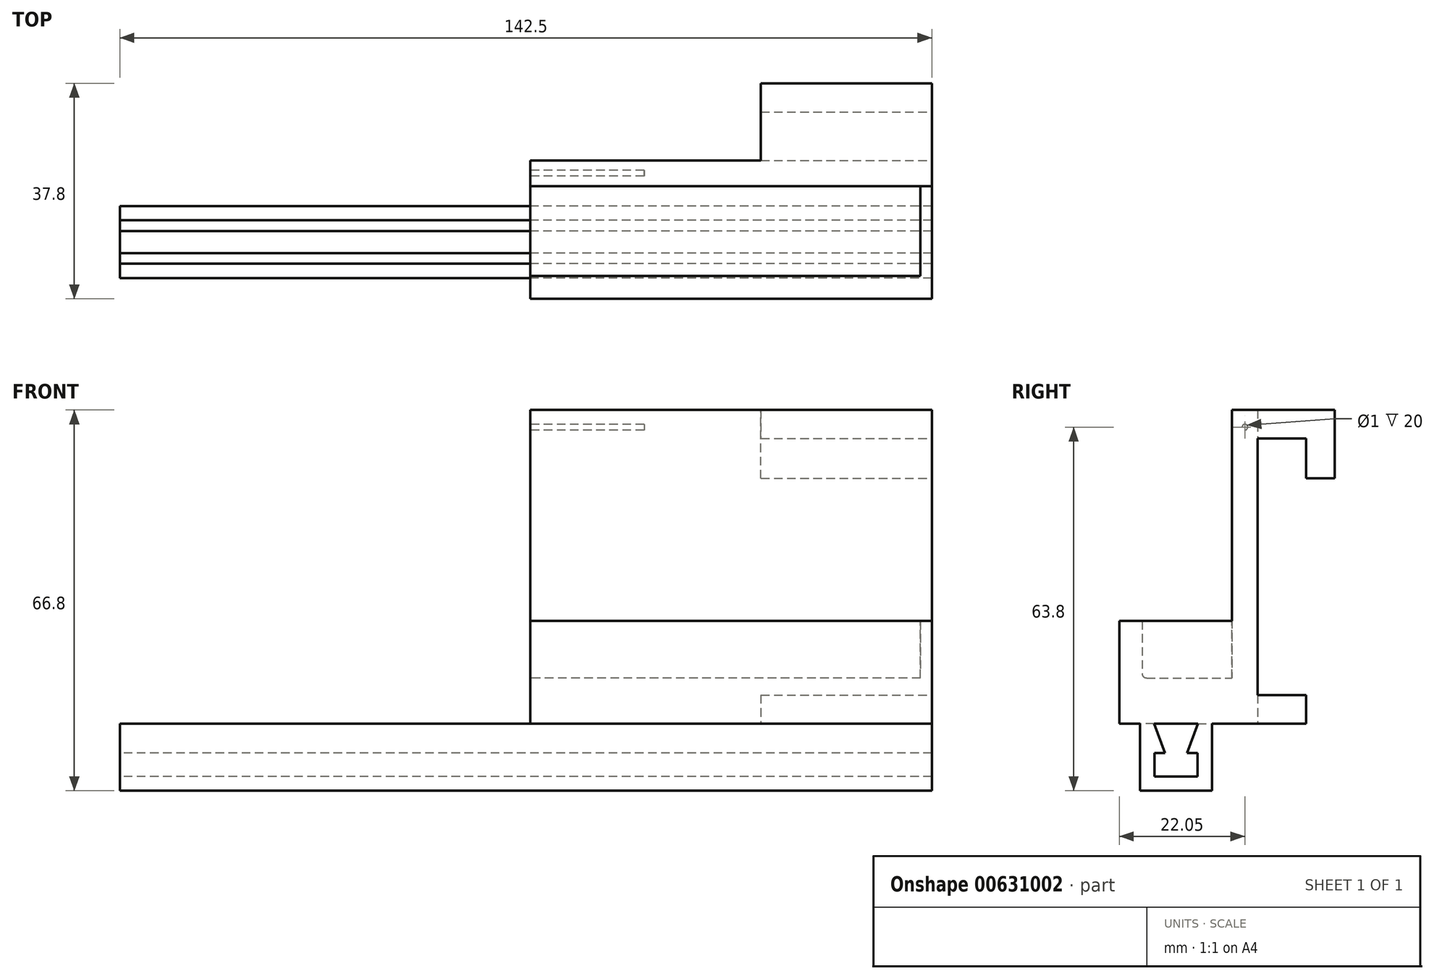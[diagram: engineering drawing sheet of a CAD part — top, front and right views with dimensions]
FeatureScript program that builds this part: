
annotation { "Feature Type Name" : "Feature", "Feature Type Description" : "" }
export const myFeature = defineFeature(function(context is Context, id is Id, definition is map)
    precondition{}
    {
        {
            var Q0;
            Q0=qCreatedBy(makeId("Front.planeOp"),FACE);
            var sketch = newSketch(context, id + "F0", { "sketchPlane" : qUnion([Q0])});
            skLineSegment(sketch, "E0.bottom", {"start": v(-77.5, -27.5) * mm, "end": v(77.5, -27.5) * mm});
            skLineSegment(sketch, "E0.top", {"start": v(-77.5, 27.5) * mm, "end": v(77.5, 27.5) * mm});
            skLineSegment(sketch, "E0.left", {"start": v(-77.5, -27.5) * mm, "end": v(-77.5, 27.5) * mm});
            skLineSegment(sketch, "E0.right", {"start": v(77.5, -27.5) * mm, "end": v(77.5, 27.5) * mm});
            skSolve(sketch);
        }
        {
            var Q0;
            Q0=makeQuery(id+"F0.imprint","IMPRINT",FACE,{"disambiguationData":[TD([[makeQuery(id+"F0.imprint","IMPRINT",EDGE,{"derivedFrom":sQuery(id+"F0.wireOp",EDGE,"E0.bottom")}),1.0]])]});
            extrude(context, id + "F1", {"entities" : qUnion([Q0]), "depth" : 13 * mm, "offsetDistance" : 25 * mm});
        }
        {
            var Q0;
            Q0=makeQuery(id+"F1.opExtrude","CAP_FACE",FACE,{"disambiguationData":[OSD([sQuery(id+"F0.wireOp",EDGE,"E0.bottom"),sQuery(id+"F0.wireOp",EDGE,"E0.top"),sQuery(id+"F0.wireOp",EDGE,"E0.left"),sQuery(id+"F0.wireOp",EDGE,"E0.right")])],"isStart":true});
            var sketch = newSketch(context, id + "F2", { "sketchPlane" : qUnion([Q0])});
            skLineSegment(sketch, "E1.bottom", {"start": v(77.5, -22.5) * mm, "end": v(47.5, -22.5) * mm});
            skLineSegment(sketch, "E1.top", {"start": v(77.5, 22.5) * mm, "end": v(47.5, 22.5) * mm});
            skLineSegment(sketch, "E1.left", {"start": v(77.5, -22.5) * mm, "end": v(77.5, 22.5) * mm});
            skLineSegment(sketch, "E1.right", {"start": v(-77.5, -22.5) * mm, "end": v(-77.5, 22.5) * mm});
            skPoint(sketch, "E1.middle", {"position": v(0, 0) * mm});
            skLineSegment(sketch, "E2.trimOffspring", {"start": v(-47.5, 22.5) * mm, "end": v(-77.5, 22.5) * mm});
            skLineSegment(sketch, "E3.trimOffspring", {"start": v(-47.5, -22.5) * mm, "end": v(-77.5, -22.5) * mm});
            skLineSegment(sketch, "E4", {"start": v(-47.5, 22.5) * mm, "end": v(47.5, 22.5) * mm});
            skLineSegment(sketch, "E5", {"start": v(-47.5, -22.5) * mm, "end": v(47.5, -22.5) * mm});
            skSolve(sketch);
        }
        {
            var Q0;
            Q0=makeQuery(id+"F2.imprint","IMPRINT",FACE,{"disambiguationData":[TD([[makeQuery(id+"F2.imprint","IMPRINT",EDGE,{"derivedFrom":sQuery(id+"F2.wireOp",EDGE,"E1.bottom")}),-1.0]])]});
            extrude(context, id + "F3", {"entities" : qUnion([Q0]), "operationType" : NewBodyOperationType.REMOVE, "oppositeDirection" : true, "depth" : 8.5 * mm, "offsetDistance" : 25 * mm});
        }
        {
            var Q0;
            Q0=makeQuery(id+"F3.boolean.opBoolean","COPY",FACE,{"derivedFrom":makeQuery(id+"F3.opExtrude","CAP_FACE",FACE,{"disambiguationData":[OSD([sQuery(id+"F2.wireOp",EDGE,"E1.bottom"),sQuery(id+"F2.wireOp",EDGE,"E1.top"),sQuery(id+"F2.wireOp",EDGE,"E1.left"),sQuery(id+"F2.wireOp",EDGE,"E1.right"),sQuery(id+"F2.wireOp",EDGE,"E2.trimOffspring"),sQuery(id+"F2.wireOp",EDGE,"E3.trimOffspring"),sQuery(id+"F2.wireOp",EDGE,"E4"),sQuery(id+"F2.wireOp",EDGE,"E5")])],"isStart":false})});
            var sketch = newSketch(context, id + "F4", { "sketchPlane" : qUnion([Q0])});
            skLineSegment(sketch, "E6", {"start": v(-47.5, 27.5) * mm, "end": v(-47.5, -27.5) * mm});
            skLineSegment(sketch, "E7", {"start": v(47.5, 27.5) * mm, "end": v(47.5, -27.5) * mm});
            skLineSegment(sketch, "E8", {"start": v(-47.5, 27.5) * mm, "end": v(47.5, 27.5) * mm});
            skLineSegment(sketch, "E9", {"start": v(-47.5, -27.5) * mm, "end": v(47.5, -27.5) * mm});
            skSolve(sketch);
        }
        {
            var Q0;
            Q0=qSketchRegion(id+"F4",true);
            extrude(context, id + "F5", {"entities" : qUnion([Q0]), "operationType" : NewBodyOperationType.REMOVE, "depth" : 8.5 * mm, "offsetDistance" : 25 * mm});
        }
        {
            var Q0;
            Q0=makeQuery(id+"F1.opExtrude","SWEPT_FACE",FACE,{"disambiguationData":[OSD([sQuery(id+"F0.wireOp",EDGE,"E0.top")])]});
            var sketch = newSketch(context, id + "F6", { "sketchPlane" : qUnion([Q0])});
            skLineSegment(sketch, "E10.bottom", {"start": v(-77.5, 0) * mm, "end": v(-47.5, 0) * mm});
            skLineSegment(sketch, "E10.top", {"start": v(-77.5, 5) * mm, "end": v(-47.5, 5) * mm});
            skLineSegment(sketch, "E10.left", {"start": v(-77.5, 0) * mm, "end": v(-77.5, 5) * mm});
            skLineSegment(sketch, "E10.right", {"start": v(-47.5, 0) * mm, "end": v(-47.5, 5) * mm});
            skLineSegment(sketch, "E11.bottom", {"start": v(47.5, 0) * mm, "end": v(77.5, 0) * mm});
            skLineSegment(sketch, "E11.top", {"start": v(47.5, 5) * mm, "end": v(77.5, 5) * mm});
            skLineSegment(sketch, "E11.left", {"start": v(47.5, 0) * mm, "end": v(47.5, 5) * mm});
            skLineSegment(sketch, "E11.right", {"start": v(77.5, 0) * mm, "end": v(77.5, 5) * mm});
            skSolve(sketch);
        }
        {
            var Q0;
            Q0=qSketchRegion(id+"F6",true);
            extrude(context, id + "F7", {"entities" : qUnion([Q0]), "operationType" : NewBodyOperationType.ADD, "oppositeDirection" : true, "depth" : (8 + 4) * mm, "offsetDistance" : 25 * mm});
        }
        {
            var Q0;
            {var subQ0=sQuery(id+"F6.wireOp",EDGE,"E10.left");Q0=makeQuery(id+"FyL1myXJDopJi9Z_1.1.F7.boolean.opBoolean","MERGE",FACE,{"derivedFrom":[makeQuery(id+"F7.boolean.opBoolean","MERGE",FACE,{"derivedFrom":[makeQuery(id+"F1.opExtrude","SWEPT_FACE",FACE,{"disambiguationData":[OSD([sQuery(id+"F0.wireOp",EDGE,"E0.left")])]}),makeQuery(id+"F7.opExtrude","SWEPT_FACE",FACE,{"disambiguationData":[OSD([subQ0])]})]}),makeQuery(id+"FyL1myXJDopJi9Z_1.1.F7.opExtrude","SWEPT_FACE",FACE,{"disambiguationData":[OSD([subQ0])]})]});}
            var sketch = newSketch(context, id + "F8", { "sketchPlane" : qUnion([Q0])});
            skLineSegment(sketch, "E12", {"start": v(13, -27.5) * mm, "end": v(28.8, -27.5) * mm});
            skLineSegment(sketch, "E13", {"start": v(28.8, -18.7) * mm, "end": v(28.8, -9.5) * mm});
            skLineSegment(sketch, "E14", {"start": v(28.8, -9.5) * mm, "end": v(32.8, -9.5) * mm});
            skLineSegment(sketch, "E15", {"start": v(32.8, -9.5) * mm, "end": v(32.8, -27.5) * mm});
            skLineSegment(sketch, "E16", {"start": v(32.8, -27.5) * mm, "end": v(28.8, -27.5) * mm});
            skLineSegment(sketch, "E17", {"start": v(13, -19.5) * mm, "end": v(28, -19.5) * mm});
            skLineSegment(sketch, "E18", {"start": v(13, -19.5) * mm, "end": v(13, -27.5) * mm});
            skPoint(sketch, "E19.visualSharp", {"position": v(28.8, -19.5) * mm});
            skArc(sketch, "E19.filletArc", {"start": v(28, -19.5) * mm, "mid": v(28.57, -19.27) * mm, "end": v(28.8, -18.7) * mm});
            skSolve(sketch);
        }
        {
            var Q0;
            Q0=makeQuery(id+"F8.imprint","IMPRINT",FACE,{"disambiguationData":[TD([[makeQuery(id+"F8.imprint","IMPRINT",EDGE,{"derivedFrom":sQuery(id+"F8.wireOp",EDGE,"E12")}),1.0]])]});
            var Q1;
            {var subQ0=sQuery(id+"F6.wireOp",EDGE,"E11.right");Q1=makeQuery(id+"FyL1myXJDopJi9Z_1.1.F7.boolean.opBoolean","MERGE",FACE,{"derivedFrom":[makeQuery(id+"F7.boolean.opBoolean","MERGE",FACE,{"derivedFrom":[makeQuery(id+"F1.opExtrude","SWEPT_FACE",FACE,{"disambiguationData":[OSD([sQuery(id+"F0.wireOp",EDGE,"E0.right")])]}),makeQuery(id+"F7.opExtrude","SWEPT_FACE",FACE,{"disambiguationData":[OSD([subQ0])]})]}),makeQuery(id+"FyL1myXJDopJi9Z_1.1.F7.opExtrude","SWEPT_FACE",FACE,{"disambiguationData":[OSD([subQ0])]})]});}
            extrude(context, id + "F9", {"entities" : qUnion([Q0]), "operationType" : NewBodyOperationType.ADD, "endBound" : BoundingType.UP_TO_SURFACE, "oppositeDirection" : true, "depth" : 25 * mm, "endBoundEntityFace" : qUnion([Q1]), "offsetDistance" : 25 * mm});
        }
        {
            var Q0;
            {var subQ0=sQuery(id+"F6.wireOp",EDGE,"E10.left");Q0=makeQuery(id+"F9.boolean.opBoolean","MERGE",FACE,{"derivedFrom":[makeQuery(id+"FyL1myXJDopJi9Z_1.1.F7.boolean.opBoolean","MERGE",FACE,{"derivedFrom":[makeQuery(id+"F7.boolean.opBoolean","MERGE",FACE,{"derivedFrom":[makeQuery(id+"F1.opExtrude","SWEPT_FACE",FACE,{"disambiguationData":[OSD([sQuery(id+"F0.wireOp",EDGE,"E0.left")])]}),makeQuery(id+"F7.opExtrude","SWEPT_FACE",FACE,{"disambiguationData":[OSD([subQ0])]})]}),makeQuery(id+"FyL1myXJDopJi9Z_1.1.F7.opExtrude","SWEPT_FACE",FACE,{"disambiguationData":[OSD([subQ0])]})]}),makeQuery(id+"F9.opExtrude","CAP_FACE",FACE,{"disambiguationData":[OSD([sQuery(id+"F8.wireOp",EDGE,"E12"),sQuery(id+"F8.wireOp",EDGE,"E13"),sQuery(id+"F8.wireOp",EDGE,"E14"),sQuery(id+"F8.wireOp",EDGE,"E15"),sQuery(id+"F8.wireOp",EDGE,"E16"),sQuery(id+"F8.wireOp",EDGE,"E17"),sQuery(id+"F8.wireOp",EDGE,"E18"),sQuery(id+"F8.wireOp",EDGE,"E19.filletArc")])],"isStart":true})]});}
            var sketch = newSketch(context, id + "F10", { "sketchPlane" : qUnion([Q0])});
            skLineSegment(sketch, "E20", {"start": v(19.33, -33) * mm, "end": v(19.33, -36.5) * mm});
            skLineSegment(sketch, "E21", {"start": v(19.33, -36.5) * mm, "end": v(26.33, -36.5) * mm});
            skLineSegment(sketch, "E22", {"start": v(26.33, -36.5) * mm, "end": v(26.33, -33) * mm});
            skLineSegment(sketch, "E23", {"start": v(26.33, -27.5) * mm, "end": v(19.33, -27.5) * mm});
            skLineSegment(sketch, "E24", {"start": v(19.33, -33) * mm, "end": v(21.33, -33) * mm});
            skLineSegment(sketch, "E25", {"start": v(21.33, -33) * mm, "end": v(19.33, -27.5) * mm});
            skLineSegment(sketch, "E26", {"start": v(22.83, -36.5) * mm, "end": v(22.83, -27.5) * mm, "construction": true});
            skLineSegment(sketch, "E27.MirrorCS", {"start": v(24.33, -33) * mm, "end": v(26.33, -27.5) * mm});
            skLineSegment(sketch, "E28.MirrorCS", {"start": v(26.33, -33) * mm, "end": v(24.33, -33) * mm});
            skLineSegment(sketch, "E29.MirrorCS", {"start": v(26.33, -33) * mm, "end": v(26.33, -36.5) * mm});
            skLineSegment(sketch, "E30", {"start": v(19.33, -33) * mm, "end": v(19.33, -36.5) * mm, "construction": true});
            skPoint(sketch, "E31.orphan", {"position": v(26.33, -27.5) * mm});
            skSolve(sketch);
        }
        {
            var Q0;
            Q0=qCreatedBy(makeId("Right.planeOp"),FACE);
            cPlane(context, id + "F11", {"entities" : qUnion([Q0]), "cplaneType" : CPlaneType.OFFSET, "offset" : 30 * mm, "oppositeDirection" : true, "width" : 150 * mm, "height" : 150 * mm});
        }
        {
            var Q0;
            Q0=qCreatedBy(id+"F11.planeOp",FACE);
            var sketch = newSketch(context, id + "F12", { "sketchPlane" : qUnion([Q0])});
            skLineSegment(sketch, "E32.0", {"start": v(-19.33, -36.5) * mm, "end": v(-26.33, -36.5) * mm, "construction": true});
            skLineSegment(sketch, "E33.0", {"start": v(-19.33, -33) * mm, "end": v(-19.33, -36.5) * mm, "construction": true});
            skLineSegment(sketch, "E34.0", {"start": v(-19.33, -33) * mm, "end": v(-21.33, -33) * mm, "construction": true});
            skLineSegment(sketch, "E35.0", {"start": v(-21.33, -33) * mm, "end": v(-19.33, -27.5) * mm, "construction": true});
            skLineSegment(sketch, "E36.0", {"start": v(-24.33, -33) * mm, "end": v(-26.33, -27.5) * mm, "construction": true});
            skLineSegment(sketch, "E37.0", {"start": v(-26.33, -33) * mm, "end": v(-24.33, -33) * mm, "construction": true});
            skLineSegment(sketch, "E38.0", {"start": v(-26.33, -33) * mm, "end": v(-26.33, -36.5) * mm, "construction": true});
            skLineSegment(sketch, "E39", {"start": v(-19.01, -27.5) * mm, "end": v(-19.33, -27.5) * mm});
            skLineSegment(sketch, "E40.0", {"start": v(-20.9, -32.7) * mm, "end": v(-19.01, -27.5) * mm});
            skLineSegment(sketch, "E41.0", {"start": v(-19.03, -32.7) * mm, "end": v(-19.03, -36.8) * mm});
            skLineSegment(sketch, "E42.0", {"start": v(-26.63, -32.7) * mm, "end": v(-26.63, -36.8) * mm});
            skLineSegment(sketch, "E43.0", {"start": v(-26.63, -32.7) * mm, "end": v(-24.76, -32.7) * mm});
            skLineSegment(sketch, "E44.0", {"start": v(-19.03, -32.7) * mm, "end": v(-20.9, -32.7) * mm});
            skLineSegment(sketch, "E45.0", {"start": v(-19.03, -36.8) * mm, "end": v(-26.63, -36.8) * mm});
            skLineSegment(sketch, "E46.trimOffspring", {"start": v(-24.76, -32.7) * mm, "end": v(-26.65, -27.5) * mm});
            skLineSegment(sketch, "E47", {"start": v(-19.01, -27.5) * mm, "end": v(-16.51, -27.5) * mm});
            skLineSegment(sketch, "E48", {"start": v(-16.51, -27.5) * mm, "end": v(-16.51, -39.3) * mm});
            skLineSegment(sketch, "E49", {"start": v(-16.51, -39.3) * mm, "end": v(-29.15, -39.3) * mm});
            skLineSegment(sketch, "E50", {"start": v(-29.15, -39.3) * mm, "end": v(-29.15, -27.5) * mm});
            skLineSegment(sketch, "E51", {"start": v(-16.51, -27.5) * mm, "end": v(-19.01, -27.5) * mm});
            skLineSegment(sketch, "E52", {"start": v(-26.65, -27.5) * mm, "end": v(-29.15, -27.5) * mm});
            skLineSegment(sketch, "E53.trimOffspring", {"start": v(-26.33, -27.5) * mm, "end": v(-26.65, -27.5) * mm});
            skSolve(sketch);
        }
        {
            var Q0;
            Q0=qSketchRegion(id+"F12",true);
            var Q1;
            {var subQ0=sQuery(id+"F6.wireOp",EDGE,"E11.right");var subQ1=sQuery(id+"F0.wireOp",EDGE,"E0.right");Q1=makeQuery(id+"F9.boolean.opBoolean","MERGE",FACE,{"derivedFrom":[makeQuery(id+"FyL1myXJDopJi9Z_1.1.F7.boolean.opBoolean","MERGE",FACE,{"derivedFrom":[makeQuery(id+"F7.boolean.opBoolean","MERGE",FACE,{"derivedFrom":[makeQuery(id+"F1.opExtrude","SWEPT_FACE",FACE,{"disambiguationData":[OSD([subQ1])]}),makeQuery(id+"F7.opExtrude","SWEPT_FACE",FACE,{"disambiguationData":[OSD([subQ0])]})]}),makeQuery(id+"FyL1myXJDopJi9Z_1.1.F7.opExtrude","SWEPT_FACE",FACE,{"disambiguationData":[OSD([subQ0])]})]}),makeQuery(id+"F9.opExtrude","CAP_FACE",FACE,{"disambiguationData":[OSD([subQ1,subQ0])],"isStart":false})]});}
            extrude(context, id + "F13", {"entities" : qUnion([Q0]), "operationType" : NewBodyOperationType.ADD, "endBound" : BoundingType.UP_TO_SURFACE, "depth" : 86.6 * mm, "endBoundEntityFace" : qUnion([Q1]), "offsetDistance" : 25 * mm});
        }
        {
            var Q0;
            Q0=makeQuery(id+"F9.opExtrude","SWEPT_FACE",FACE,{"disambiguationData":[OSD([sQuery(id+"F8.wireOp",EDGE,"E15")])]});
            var sketch = newSketch(context, id + "F14", { "sketchPlane" : qUnion([Q0])});
            skLineSegment(sketch, "E54.bottom", {"start": v(33.5, 67.48) * mm, "end": v(115.57, 67.48) * mm});
            skLineSegment(sketch, "E54.top", {"start": v(33.5, -48.03) * mm, "end": v(115.57, -48.03) * mm});
            skLineSegment(sketch, "E54.left", {"start": v(33.5, 67.48) * mm, "end": v(33.5, -48.03) * mm});
            skLineSegment(sketch, "E54.right", {"start": v(115.57, 67.48) * mm, "end": v(115.57, -48.03) * mm});
            skSolve(sketch);
        }
        {
            var Q0;
            {var subQ1=sQuery(id+"F8.wireOp",EDGE,"E15");var subQ6=makeQuery(id+"F9.opExtrude","CAP_EDGE",EDGE,{"disambiguationData":[OSD([subQ1])],"isStart":true});Q0=makeQuery(id+"F14.imprint","IMPRINT",FACE,{"disambiguationData":[TD([[makeQuery(id+"F14.imprint","IMPRINT",EDGE,{"derivedFrom":subQ6}),1.0]])]});}
            var sketch = newSketch(context, id + "F15", { "sketchPlane" : qUnion([Q0])});
            skLineSegment(sketch, "E55.bottom", {"start": v(-107.56, 91.1) * mm, "end": v(7, 91.1) * mm});
            skLineSegment(sketch, "E55.top", {"start": v(-107.56, -27.5) * mm, "end": v(7, -27.5) * mm});
            skLineSegment(sketch, "E55.left", {"start": v(-107.56, 91.1) * mm, "end": v(-107.56, -27.5) * mm});
            skLineSegment(sketch, "E55.right", {"start": v(7, 91.1) * mm, "end": v(7, -27.5) * mm});
            skSolve(sketch);
        }
        {
            var Q0;
            Q0 = qSketchRegion(id + "F15", true);
            extrude(context, id + "F16", {"entities" : qUnion([Q0]), "operationType" : NewBodyOperationType.REMOVE, "oppositeDirection" : true, "depth" : 53.7 * mm, "offsetDistance" : 25 * mm});
        }
        {
            var Q0;
            Q0=makeQuery(id+"F16.boolean.opBoolean","COPY",FACE,{"derivedFrom":makeQuery(id+"F16.opExtrude","SWEPT_FACE",FACE,{"disambiguationData":[OSD([sQuery(id+"F15.wireOp",EDGE,"E55.right")])]})});
            var sketch = newSketch(context, id + "F17", { "sketchPlane" : qUnion([Q0])});
            skCircle(sketch, "E56", {"center": v(10.75, 24.5) * mm, "radius": 0.5 * mm});
            skPoint(sketch, "E57", {"position": v(10.75, 27.5) * mm});
            skSolve(sketch);
        }
        {
            var Q0;
            Q0 = qSketchRegion(id + "F17", true);
            extrude(context, id + "F18", {"entities" : qUnion([Q0]), "operationType" : NewBodyOperationType.REMOVE, "oppositeDirection" : true, "depth" : 20 * mm, "offsetDistance" : 25 * mm});
        }
        {
            var Q0;
            Q0=makeQuery(id+"F13.opExtrude","CAP_FACE",FACE,{"disambiguationData":[OSD([sQuery(id+"F12.wireOp",EDGE,"E40.0"),sQuery(id+"F12.wireOp",EDGE,"E41.0"),sQuery(id+"F12.wireOp",EDGE,"E42.0"),sQuery(id+"F12.wireOp",EDGE,"E43.0"),sQuery(id+"F12.wireOp",EDGE,"E44.0"),sQuery(id+"F12.wireOp",EDGE,"E45.0"),sQuery(id+"F12.wireOp",EDGE,"E46.trimOffspring"),sQuery(id+"F12.wireOp",EDGE,"E48"),sQuery(id+"F12.wireOp",EDGE,"E49"),sQuery(id+"F12.wireOp",EDGE,"E50"),sQuery(id+"F12.wireOp",EDGE,"E51"),sQuery(id+"F12.wireOp",EDGE,"E52")])],"isStart":true});
            extrude(context, id + "F19", {"entities" : qUnion([Q0]), "operationType" : NewBodyOperationType.ADD, "depth" : 35 * mm, "offsetDistance" : 25 * mm});
        }
        {
            var Q0;
            {var subQ0=sQuery(id+"F6.wireOp",EDGE,"E11.right");var subQ1=sQuery(id+"F0.wireOp",EDGE,"E0.right");Q0=makeQuery(id+"F13.boolean.opBoolean","MERGE",FACE,{"derivedFrom":[makeQuery(id+"F9.boolean.opBoolean","MERGE",FACE,{"derivedFrom":[makeQuery(id+"FyL1myXJDopJi9Z_1.1.F7.boolean.opBoolean","MERGE",FACE,{"derivedFrom":[makeQuery(id+"F7.boolean.opBoolean","MERGE",FACE,{"derivedFrom":[makeQuery(id+"F1.opExtrude","SWEPT_FACE",FACE,{"disambiguationData":[OSD([subQ1])]}),makeQuery(id+"F7.opExtrude","SWEPT_FACE",FACE,{"disambiguationData":[OSD([subQ0])]})]}),makeQuery(id+"FyL1myXJDopJi9Z_1.1.F7.opExtrude","SWEPT_FACE",FACE,{"disambiguationData":[OSD([subQ0])]})]}),makeQuery(id+"F9.opExtrude","CAP_FACE",FACE,{"disambiguationData":[OSD([subQ1,subQ0])],"isStart":false})]}),makeQuery(id+"F13.opExtrude","CAP_FACE",FACE,{"disambiguationData":[OSD([subQ1,subQ0])],"isStart":false})]});}
            var sketch = newSketch(context, id + "F20", { "sketchPlane" : qUnion([Q0])});
            skLineSegment(sketch, "E58.0", {"start": v(-28.8, -9.5) * mm, "end": v(-28.8, -18.7) * mm});
            skArc(sketch, "E59.0", {"start": v(-28.8, -18.7) * mm, "mid": v(-28.57, -19.27) * mm, "end": v(-28, -19.5) * mm});
            skLineSegment(sketch, "E60.0", {"start": v(-28, -19.5) * mm, "end": v(-13, -19.5) * mm});
            skLineSegment(sketch, "E61.0", {"start": v(-13, -19.5) * mm, "end": v(-13, -9.5) * mm});
            skLineSegment(sketch, "E62", {"start": v(-28.8, -9.5) * mm, "end": v(-13, -9.5) * mm});
            skPoint(sketch, "E63.orphan", {"position": v(-13, 27.5) * mm});
            skSolve(sketch);
        }
        {
            var Q0;
            Q0 = qSketchRegion(id + "F20", true);
            extrude(context, id + "F21", {"entities" : qUnion([Q0]), "operationType" : NewBodyOperationType.ADD, "oppositeDirection" : true, "depth" : 2 * mm, "offsetDistance" : 25 * mm});
        }
    });
